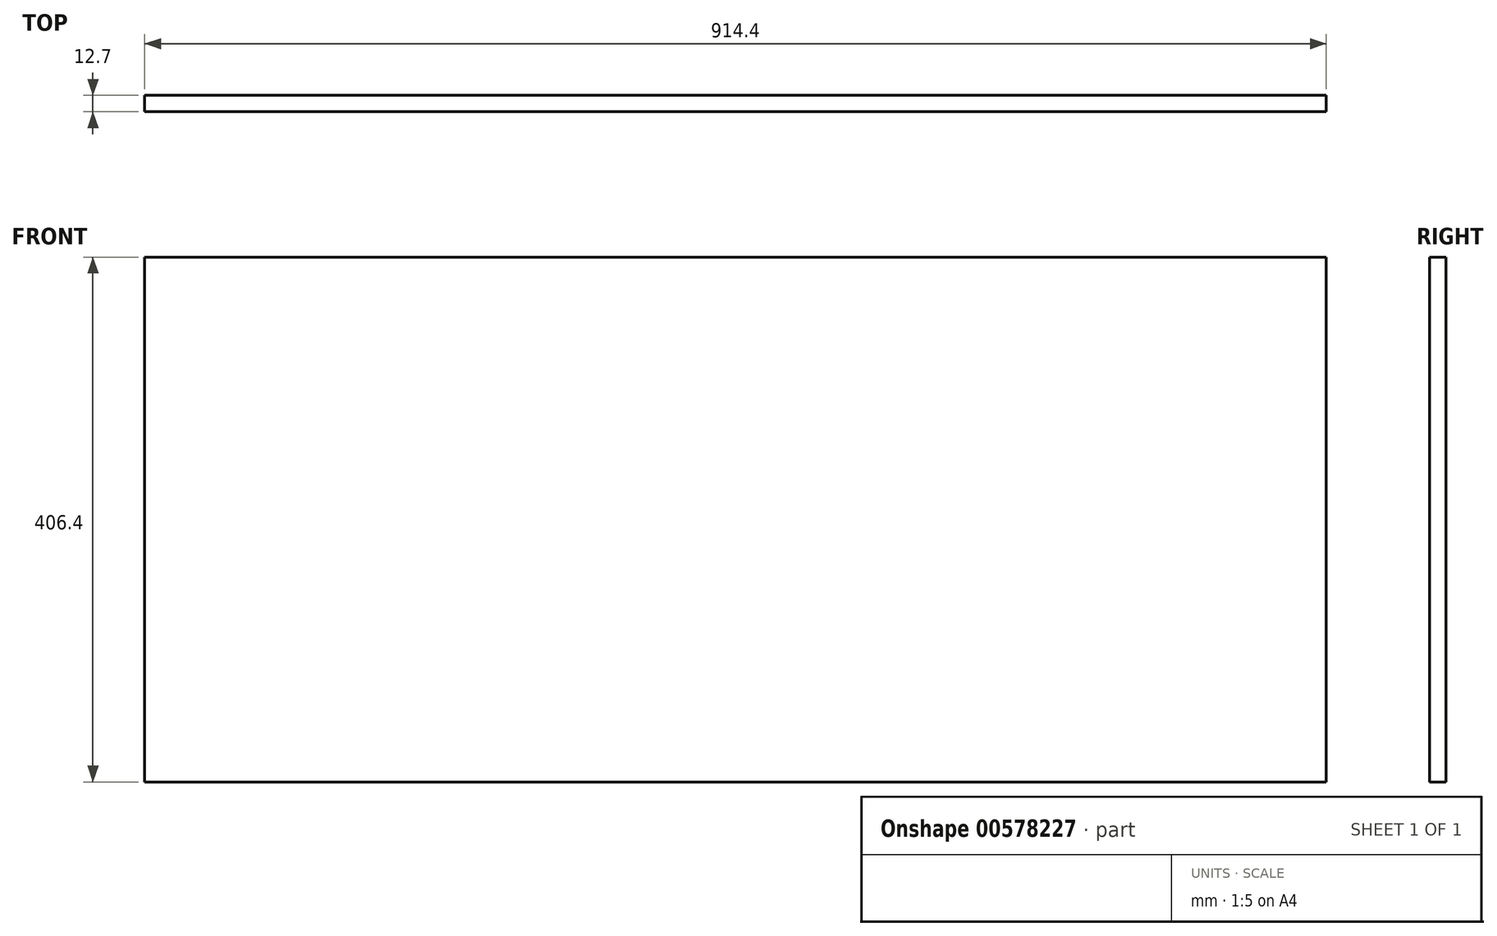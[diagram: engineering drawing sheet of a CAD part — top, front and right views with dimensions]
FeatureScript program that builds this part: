
annotation { "Feature Type Name" : "Feature", "Feature Type Description" : "" }
export const myFeature = defineFeature(function(context is Context, id is Id, definition is map)
    precondition{}
    {
        {
            var Q0;
            Q0=qCreatedBy(makeId("Front.planeOp"),FACE);
            var sketch = newSketch(context, id + "F0", { "sketchPlane" : qUnion([Q0])});
            skLineSegment(sketch, "E0.bottom", {"start": v(-875.3, 380.38) * mm, "end": v(39.1, 380.38) * mm});
            skLineSegment(sketch, "E0.top", {"start": v(-875.3, -26.02) * mm, "end": v(39.1, -26.02) * mm});
            skLineSegment(sketch, "E0.left", {"start": v(-875.3, 380.38) * mm, "end": v(-875.3, -26.02) * mm});
            skLineSegment(sketch, "E0.right", {"start": v(39.1, 380.38) * mm, "end": v(39.1, -26.02) * mm});
            skSolve(sketch);
        }
        {
            var Q0;
            Q0 = qSketchRegion(id + "F0", true);
            extrude(context, id + "F1", {"entities" : qUnion([Q0]), "depth" : 12.7 * mm, "offsetDistance" : 25.4 * mm});
        }
    });
